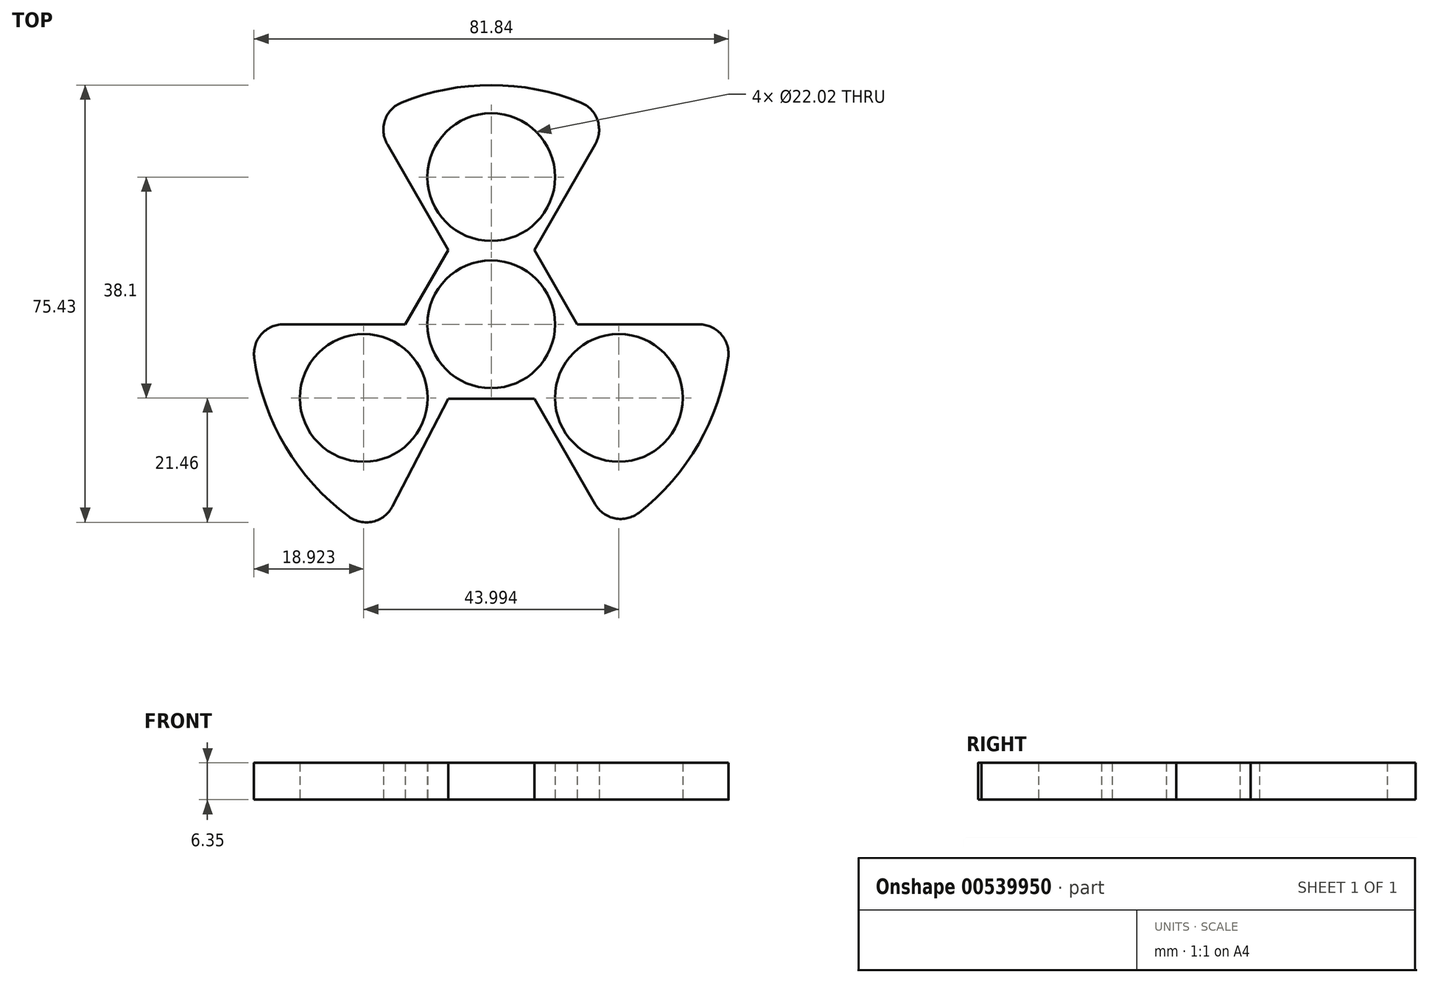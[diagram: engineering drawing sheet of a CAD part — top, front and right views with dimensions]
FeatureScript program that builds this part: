
annotation { "Feature Type Name" : "Feature", "Feature Type Description" : "" }
export const myFeature = defineFeature(function(context is Context, id is Id, definition is map)
    precondition{}
    {
        {
            var Q0;
            Q0=qCreatedBy(makeId("Top.planeOp"),FACE);
            var sketch = newSketch(context, id + "F0", { "sketchPlane" : qUnion([Q0])});
            skCircle(sketch, "E0", {"center": v(0, 0) * mm, "radius": 11.01 * mm});
            skCircle(sketch, "E1", {"center": v(0, 0) * mm, "radius": 41.28 * mm});
            skCircle(sketch, "E2", {"center": v(0, 25.4) * mm, "radius": 11.01 * mm});
            skCircle(sketch, "E3.1.0", {"center": v(-22, -12.7) * mm, "radius": 11.01 * mm});
            skCircle(sketch, "E3.2.0", {"center": v(22, -12.7) * mm, "radius": 11.01 * mm});
            skCircle(sketch, "E4.cCircle", {"center": v(0, 0) * mm, "radius": 12.85 * mm, "construction": true});
            skLineSegment(sketch, "E4.0", {"start": v(-7.42, 12.85) * mm, "end": v(7.42, 12.85) * mm});
            skLineSegment(sketch, "E4.1", {"start": v(7.42, 12.85) * mm, "end": v(14.84, 0) * mm});
            skLineSegment(sketch, "E4.2", {"start": v(14.84, 0) * mm, "end": v(7.42, -12.85) * mm});
            skLineSegment(sketch, "E4.3", {"start": v(7.42, -12.85) * mm, "end": v(-7.42, -12.85) * mm});
            skLineSegment(sketch, "E4.4", {"start": v(-7.42, -12.85) * mm, "end": v(-14.84, 0) * mm});
            skLineSegment(sketch, "E4.5", {"start": v(-14.84, 0) * mm, "end": v(-7.42, 12.85) * mm});
            skPoint(sketch, "E4.0.midPoint", {"position": v(0, 12.85) * mm});
            skLineSegment(sketch, "E5", {"start": v(7.42, 12.85) * mm, "end": v(20.64, 35.75) * mm});
            skLineSegment(sketch, "E6", {"start": v(-7.42, 12.85) * mm, "end": v(-20.64, 35.75) * mm});
            skLineSegment(sketch, "E7", {"start": v(-14.84, 0) * mm, "end": v(-41.28, 0) * mm});
            skLineSegment(sketch, "E8", {"start": v(-7.42, -12.85) * mm, "end": v(-19.59, -36.33) * mm});
            skLineSegment(sketch, "E9", {"start": v(7.42, -12.85) * mm, "end": v(20.64, -35.75) * mm});
            skLineSegment(sketch, "E10", {"start": v(14.84, 0) * mm, "end": v(41.28, 0) * mm});
            skSolve(sketch);
        }
        {
            var Q0;
            Q0=makeQuery(id+"F0.imprint","IMPRINT",FACE,{"disambiguationData":[TD([[makeQuery(id+"F0.imprint","IMPRINT",EDGE,{"derivedFrom":sQuery(id+"F0.wireOp",EDGE,"E0")}),-1.0]])]});
            var Q1;
            Q1=makeQuery(id+"F0.imprint","IMPRINT",FACE,{"disambiguationData":[TD([[makeQuery(id+"F0.imprint","IMPRINT",EDGE,{"derivedFrom":sQuery(id+"F0.wireOp",EDGE,"E3.2.0")}),-1.0]])]});
            var Q2;
            Q2=makeQuery(id+"F0.imprint","IMPRINT",FACE,{"disambiguationData":[TD([[makeQuery(id+"F0.imprint","IMPRINT",EDGE,{"derivedFrom":sQuery(id+"F0.wireOp",EDGE,"E3.1.0")}),-1.0]])]});
            var Q3;
            Q3=makeQuery(id+"F0.imprint","IMPRINT",FACE,{"disambiguationData":[TD([[makeQuery(id+"F0.imprint","IMPRINT",EDGE,{"derivedFrom":sQuery(id+"F0.wireOp",EDGE,"E2")}),-1.0]])]});
            extrude(context, id + "F1", {"entities" : qUnion([Q0, Q1, Q2, Q3]), "depth" : 6.35 * mm, "offsetDistance" : 25.4 * mm});
        }
        {
            var Q0;
            Q0=makeQuery(id+"F1.opExtrude","SWEPT_EDGE",EDGE,{"disambiguationData":[OSD([sQuery(id+"F0.wireOp",EDGE,"E1"),sQuery(id+"F0.wireOp",EDGE,"E8")])]});
            fillet(context, id + "F2", {"entities" : qUnion([Q0]), "radius" : 5.08 * mm, "tangentPropagation" : true, "allowEdgeOverflow" : false});
        }
        {
            var Q0;
            Q0=makeQuery(id+"F1.opExtrude","SWEPT_EDGE",EDGE,{"disambiguationData":[OSD([sQuery(id+"F0.wireOp",EDGE,"E1"),sQuery(id+"F0.wireOp",EDGE,"E9")])]});
            fillet(context, id + "F3", {"entities" : qUnion([Q0]), "radius" : 5.08 * mm, "tangentPropagation" : true, "allowEdgeOverflow" : false});
        }
        {
            var Q0;
            Q0=makeQuery(id+"F1.opExtrude","SWEPT_EDGE",EDGE,{"disambiguationData":[OSD([sQuery(id+"F0.wireOp",EDGE,"E1"),sQuery(id+"F0.wireOp",EDGE,"E7")])]});
            fillet(context, id + "F4", {"entities" : qUnion([Q0]), "radius" : 5.08 * mm, "tangentPropagation" : true, "allowEdgeOverflow" : false});
        }
        {
            var Q0;
            Q0=makeQuery(id+"F1.opExtrude","SWEPT_EDGE",EDGE,{"disambiguationData":[OSD([sQuery(id+"F0.wireOp",EDGE,"E1"),sQuery(id+"F0.wireOp",EDGE,"E6")])]});
            fillet(context, id + "F5", {"entities" : qUnion([Q0]), "radius" : 5.08 * mm, "tangentPropagation" : true, "allowEdgeOverflow" : false});
        }
        {
            var Q0;
            Q0=makeQuery(id+"F1.opExtrude","SWEPT_EDGE",EDGE,{"disambiguationData":[OSD([sQuery(id+"F0.wireOp",EDGE,"E1"),sQuery(id+"F0.wireOp",EDGE,"E10")])]});
            fillet(context, id + "F6", {"entities" : qUnion([Q0]), "radius" : 5.08 * mm, "tangentPropagation" : true, "allowEdgeOverflow" : false});
        }
        {
            var Q0;
            Q0=makeQuery(id+"F1.opExtrude","SWEPT_EDGE",EDGE,{"disambiguationData":[OSD([sQuery(id+"F0.wireOp",EDGE,"E1"),sQuery(id+"F0.wireOp",EDGE,"E5")])]});
            fillet(context, id + "F7", {"entities" : qUnion([Q0]), "radius" : 5.08 * mm, "tangentPropagation" : true, "allowEdgeOverflow" : false});
        }
    });
